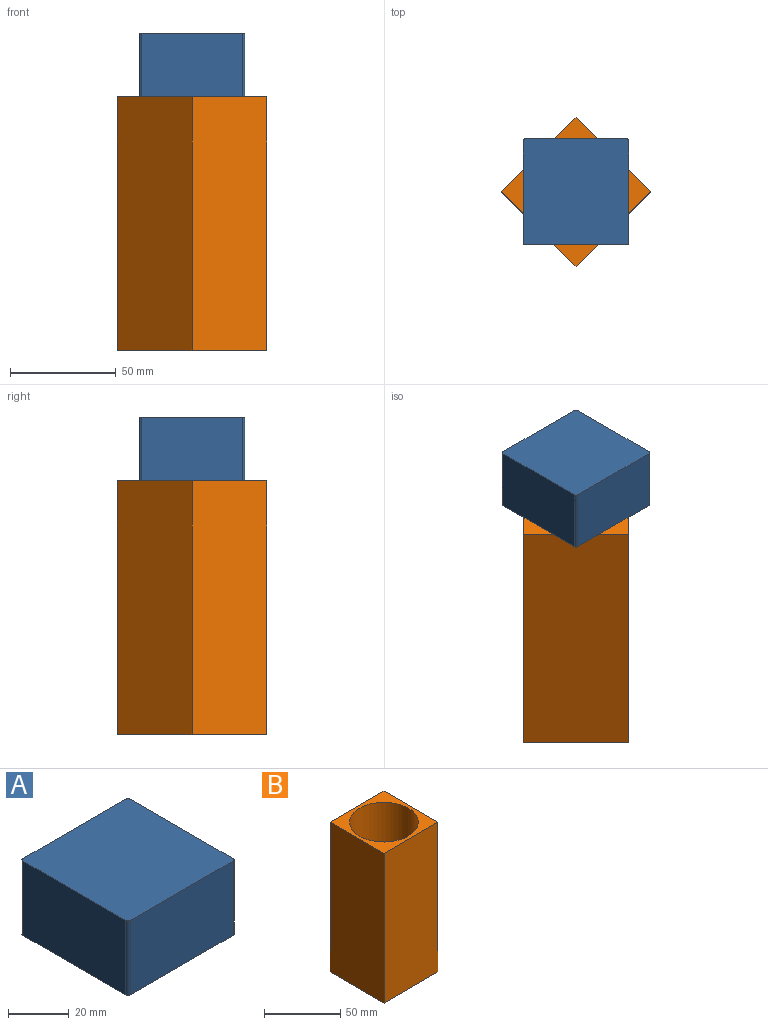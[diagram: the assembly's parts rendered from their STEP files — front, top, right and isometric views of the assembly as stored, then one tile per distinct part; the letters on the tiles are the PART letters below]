
ASSEMBLY  parts=2 mates=1
PART A: 10 faces, bbox 50x50x30 mm
  f0: plane 48x30mm, normal (1,0,0), area 1440mm2, adj f1,f7,f8,f9
  f1: cylinder r=1mm len=30mm, axis (0,0,-1), area 47.1mm2, adj f0,f2,f8,f9
  f2: plane 48x30mm, normal (0,1,0), area 1440mm2, adj f1,f3,f8,f9
  f3: cylinder r=1mm len=30mm, axis (0,0,-1), area 47.1mm2, adj f2,f4,f8,f9
  f4: plane 48x30mm, normal (-1,0,0), area 1440mm2, adj f3,f5,f8,f9
  f5: cylinder r=1mm len=30mm, axis (0,0,-1), area 47.1mm2, adj f4,f6,f8,f9
  f6: plane 48x30mm, normal (0,-1,0), area 1440mm2, adj f5,f7,f8,f9
  f7: cylinder r=1mm len=30mm, axis (0,0,-1), area 47.1mm2, adj f0,f6,f8,f9
  f8: plane 50x50mm, normal (0,0,1), area 2499.1mm2, adj f0,f1,f2,f3,f4,f5,f6,f7
  f9: plane 50x50mm, normal (0,0,-1), area 2499.1mm2, adj f0,f1,f2,f3,f4,f5,f6,f7
PART B: 8 faces, bbox 50x50x120 mm
  f0: plane 45x45mm, normal (0,0,1), area 1590.4mm2, adj f5
  f1: plane 120x50mm, normal (1,0,0), area 6000mm2, adj f2,f4,f6,f7
  f2: plane 120x50mm, normal (0,1,0), area 6000mm2, adj f1,f3,f6,f7
  f3: plane 120x50mm, normal (-1,0,0), area 6000mm2, adj f2,f4,f6,f7
  f4: plane 120x50mm, normal (0,-1,0), area 6000mm2, adj f1,f3,f6,f7
  f5: cylinder r=22.5mm len=115mm, axis (0,0,-1), area 16257.7mm2, adj f0,f6
  f6: plane 50x50mm, normal (0,0,1), area 909.6mm2, adj f1,f2,f3,f4,f5
  f7: plane 50x50mm, normal (0,0,-1), area 2500mm2, adj f1,f2,f3,f4
PLACE A rot(axis=(0,0,1),0deg) t=(-89.87,-20.54,28.19)mm
PLACE B rot(axis=(0,0,-1),45deg) t=(-89.87,-20.54,-91.81)mm
MATE revolute B.f5 <-> A.f9  axis (0,0,-1) through (-89.87,-20.54,28.19)mm
